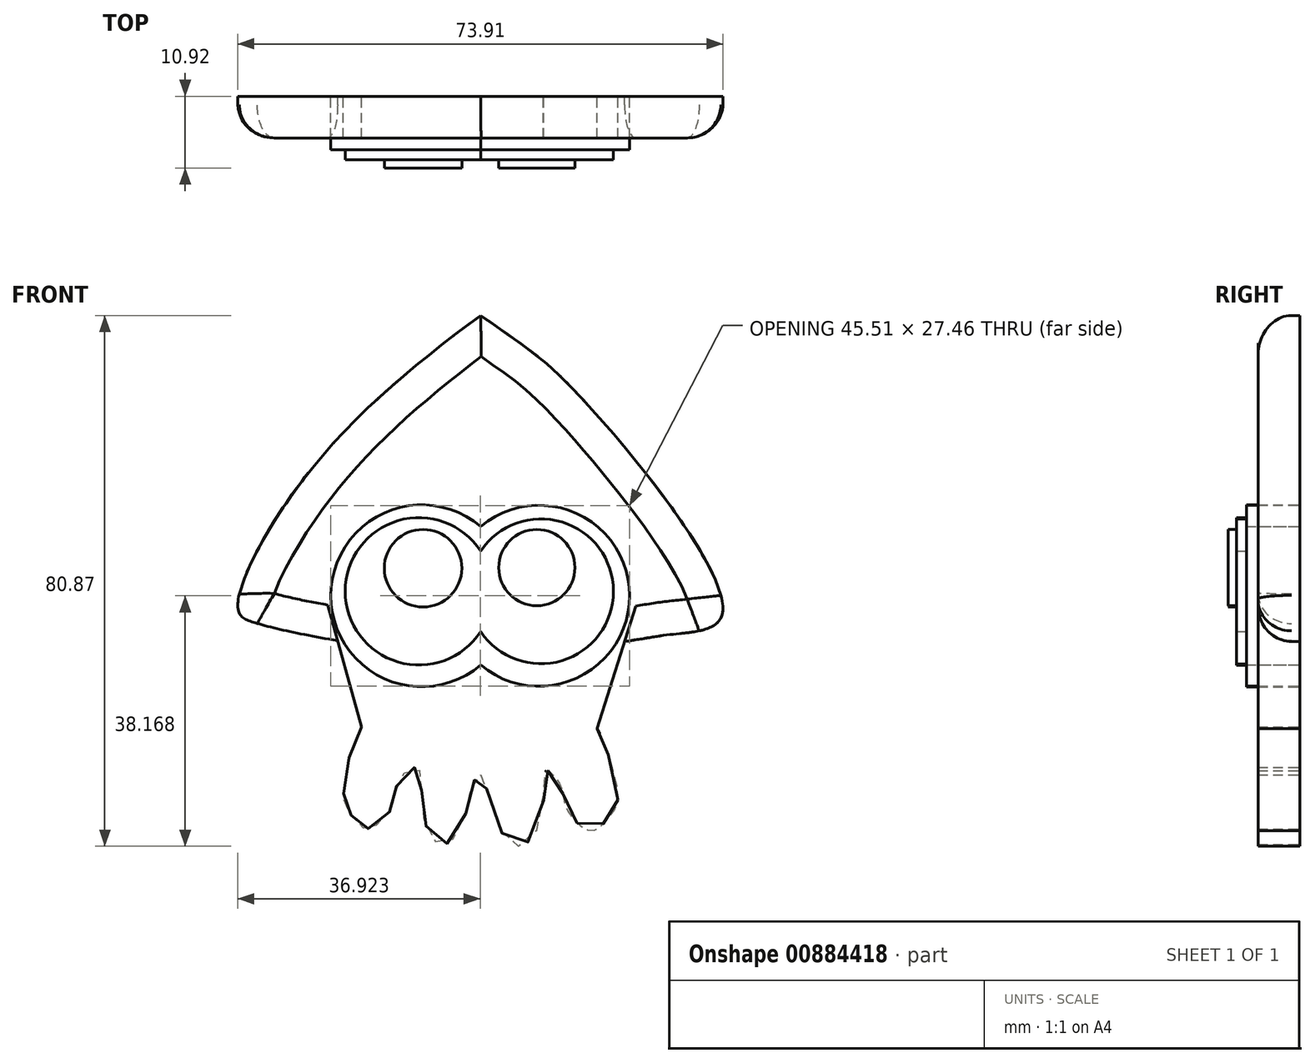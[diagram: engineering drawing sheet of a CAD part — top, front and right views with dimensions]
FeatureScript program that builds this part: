
annotation { "Feature Type Name" : "Feature", "Feature Type Description" : "" }
export const myFeature = defineFeature(function(context is Context, id is Id, definition is map)
    precondition{}
    {
        {
            var Q0;
            Q0=qCreatedBy(makeId("Front.planeOp"),FACE);
            var sketch = newSketch(context, id + "F0", { "sketchPlane" : qUnion([Q0])});
            skFitSpline(sketch, "E0", {"points": [v(0, 51.1) * mm, v(-8.4, 44.66) * mm, v(-26.98, 26.2) * mm, v(-36.97, 6.37) * mm, v(-34.19, 4.22) * mm, v(-21.8, 1.57) * mm], "startDerivative": vector(-46.48, -33.45) * mm, "endDerivative": vector(81.5, -13.63) * mm});
            skFitSpline(sketch, "E1", {"points": [v(0, 51.1) * mm, v(5.74, 47.06) * mm, v(14.46, 39.48) * mm, v(36.83, 5.74) * mm, v(29.62, 2.58) * mm, v(21.92, 1.44) * mm], "startDerivative": vector(47.67, -31.92) * mm, "endDerivative": vector(-59.4, -8.07) * mm});
            skLineSegment(sketch, "E2", {"start": v(-21.8, 1.57) * mm, "end": v(-18.14, -11.57) * mm});
            skLineSegment(sketch, "E3", {"start": v(21.92, 1.44) * mm, "end": v(17.75, -11.82) * mm});
            skFitSpline(sketch, "E4", {"points": [v(-18.14, -11.57) * mm, v(-20.03, -16.25) * mm, v(-20.92, -21.93) * mm, v(-20.54, -23.96) * mm, v(-18.14, -26.74) * mm, v(-17.25, -27.11) * mm, v(-14.6, -25.47) * mm, v(-12.96, -22.06) * mm, v(-12.45, -19.53) * mm, v(-9.8, -17.76) * mm, v(-9.04, -20.3) * mm, v(-8.54, -26.1) * mm, v(-5.88, -29.52) * mm, v(-2.72, -26.23) * mm, v(-1.2, -20.3) * mm, v(0, -18.9) * mm, v(1.83, -24.59) * mm, v(5.74, -29.77) * mm, v(9.4, -24.59) * mm, v(9.91, -18.27) * mm, v(12.06, -20.3) * mm, v(12.95, -23.7) * mm, v(16.74, -27.37) * mm, v(19.64, -25.22) * mm, v(20.9, -22.06) * mm, v(18.38, -13.09) * mm, v(17.75, -11.82) * mm], "startDerivative": vector(-48.86, -99.74) * mm, "endDerivative": vector(-21.63, 36.47) * mm});
            skArc(sketch, "E5", {"start": v(0, 15.2) * mm, "mid": v(-20.64, 9.07) * mm, "end": v(0, 2.95) * mm});
            skArc(sketch, "E6", {"start": v(0, 2.95) * mm, "mid": v(20.22, 9.07) * mm, "end": v(0, 15.2) * mm});
            skArc(sketch, "E7", {"start": v(0, -2.15) * mm, "mid": v(22.67, 8.4) * mm, "end": v(0, 18.94) * mm});
            skArc(sketch, "E8", {"start": v(0, 18.94) * mm, "mid": v(-22.84, 8.4) * mm, "end": v(0, -2.15) * mm});
            skCircle(sketch, "E9", {"center": v(-8.78, 12.6) * mm, "radius": 5.91 * mm});
            skPoint(sketch, "E9.first.point", {"position": v(-13.53, 9.08) * mm});
            skPoint(sketch, "E9.second.point", {"position": v(-4.07, 16.17) * mm});
            skPoint(sketch, "E9.third.point", {"position": v(-7.05, 18.25) * mm});
            skCircle(sketch, "E10", {"center": v(8.55, 12.7) * mm, "radius": 5.8 * mm});
            skPoint(sketch, "E10.first.point", {"position": v(3.42, 9.98) * mm});
            skPoint(sketch, "E10.second.point", {"position": v(13.66, 15.44) * mm});
            skPoint(sketch, "E10.third.point", {"position": v(12.42, 17.01) * mm});
            skSolve(sketch);
        }
        {
            var Q0;
            Q0=makeQuery(id+"F0.imprint","IMPRINT",FACE,{"disambiguationData":[TD([[makeQuery(id+"F0.imprint","IMPRINT",EDGE,{"derivedFrom":sQuery(id+"F0.wireOp",EDGE,"E0")}),1.0]])]});
            extrude(context, id + "F1", {"entities" : qUnion([Q0]), "depth" : 6.35 * mm, "offsetDistance" : 25.4 * mm});
        }
        {
            var Q0;
            Q0=makeQuery(id+"F0.imprint","IMPRINT",FACE,{"disambiguationData":[TD([[makeQuery(id+"F0.imprint","IMPRINT",EDGE,{"derivedFrom":sQuery(id+"F0.wireOp",EDGE,"E5")}),-1.0]])]});
            extrude(context, id + "F2", {"entities" : qUnion([Q0]), "depth" : 8.13 * mm, "offsetDistance" : 25.4 * mm});
        }
        {
            var Q0;
            Q0=makeQuery(id+"F0.imprint","IMPRINT",FACE,{"disambiguationData":[TD([[makeQuery(id+"F0.imprint","IMPRINT",EDGE,{"derivedFrom":sQuery(id+"F0.wireOp",EDGE,"E5")}),1.0]])]});
            extrude(context, id + "F3", {"entities" : qUnion([Q0]), "operationType" : NewBodyOperationType.ADD, "depth" : 9.65 * mm, "offsetDistance" : 25.4 * mm});
        }
        {
            var Q0;
            Q0=makeQuery(id+"F0.imprint","IMPRINT",FACE,{"disambiguationData":[TD([[makeQuery(id+"F0.imprint","IMPRINT",EDGE,{"derivedFrom":sQuery(id+"F0.wireOp",EDGE,"E9")}),1.0]])]});
            var Q1;
            Q1=makeQuery(id+"F0.imprint","IMPRINT",FACE,{"disambiguationData":[TD([[makeQuery(id+"F0.imprint","IMPRINT",EDGE,{"derivedFrom":sQuery(id+"F0.wireOp",EDGE,"E10")}),1.0]])]});
            extrude(context, id + "F4", {"entities" : qUnion([Q0, Q1]), "operationType" : NewBodyOperationType.ADD, "depth" : 10.92 * mm, "offsetDistance" : 25.4 * mm});
        }
        {
            var Q0;
            Q0=makeQuery(id+"F1.opExtrude","CAP_EDGE",EDGE,{"disambiguationData":[OSD([sQuery(id+"F0.wireOp",EDGE,"E0")])],"isStart":false});
            var Q1;
            Q1=makeQuery(id+"F1.opExtrude","CAP_EDGE",EDGE,{"disambiguationData":[OSD([sQuery(id+"F0.wireOp",EDGE,"E1")])],"isStart":false});
            fillet(context, id + "F5", {"entities" : qUnion([Q0, Q1]), "radius" : 5.08 * mm, "tangentPropagation" : true, "allowEdgeOverflow" : false});
        }
    });
